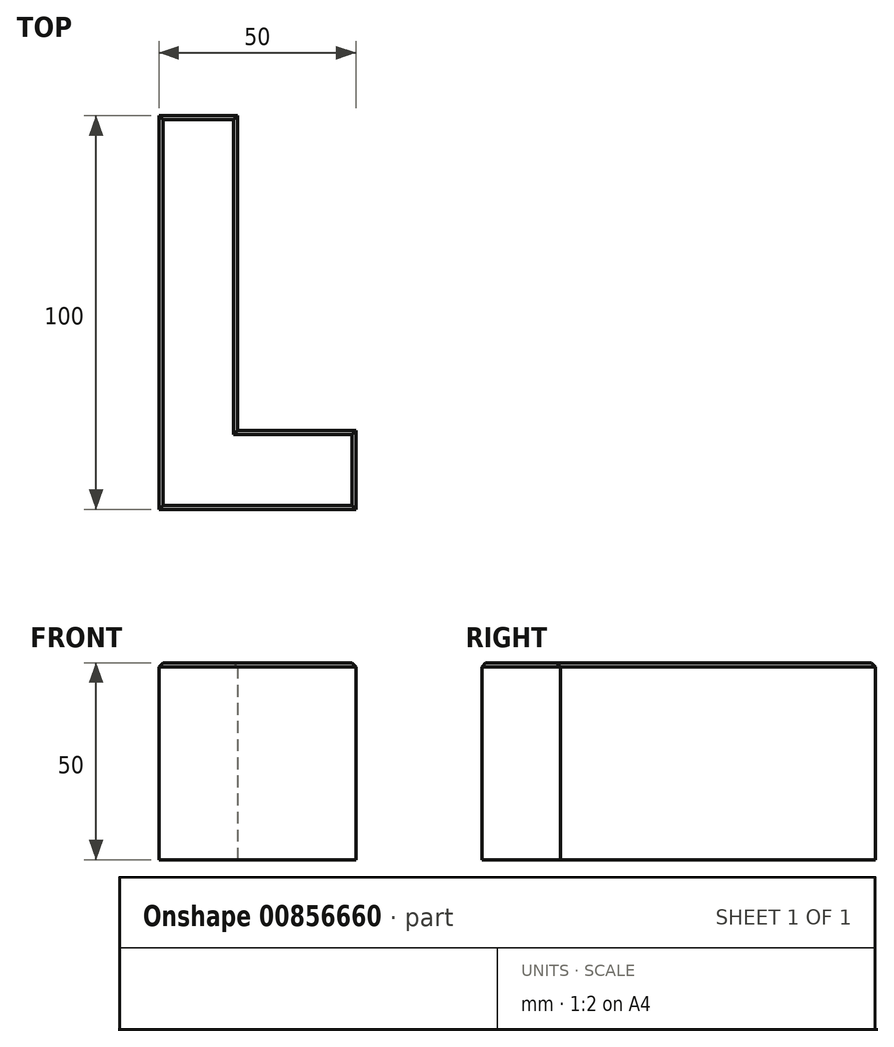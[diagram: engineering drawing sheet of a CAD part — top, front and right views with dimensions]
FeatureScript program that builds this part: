
annotation { "Feature Type Name" : "Feature", "Feature Type Description" : "" }
export const myFeature = defineFeature(function(context is Context, id is Id, definition is map)
    precondition{}
    {
        {
            var Q0;
            Q0=qCreatedBy(makeId("Top.planeOp"),FACE);
            var sketch = newSketch(context, id + "F0", { "sketchPlane" : qUnion([Q0])});
            skLineSegment(sketch, "E0", {"start": v(-67.67, -40.21) * mm, "end": v(-17.67, -40.21) * mm});
            skLineSegment(sketch, "E1", {"start": v(-67.67, -40.21) * mm, "end": v(-67.67, 59.79) * mm});
            skLineSegment(sketch, "E2", {"start": v(-17.67, -40.21) * mm, "end": v(-17.67, -20.21) * mm});
            skLineSegment(sketch, "E3", {"start": v(-67.67, 59.79) * mm, "end": v(-47.67, 59.79) * mm});
            skLineSegment(sketch, "E4", {"start": v(-47.67, 59.79) * mm, "end": v(-47.67, -20.21) * mm});
            skLineSegment(sketch, "E5", {"start": v(-17.67, -20.21) * mm, "end": v(-47.67, -20.21) * mm});
            skSolve(sketch);
        }
        {
            var Q0;
            Q0=makeQuery(id+"F0.imprint","IMPRINT",FACE,{"disambiguationData":[TD([[makeQuery(id+"F0.imprint","IMPRINT",EDGE,{"derivedFrom":sQuery(id+"F0.wireOp",EDGE,"E0")}),1.0]])]});
            extrude(context, id + "F1", {"entities" : qUnion([Q0]), "depth" : 50 * mm, "offsetDistance" : 25 * mm});
        }
        {
            var Q0;
            Q0=makeQuery(id+"F1.opExtrude","CAP_EDGE",EDGE,{"disambiguationData":[OSD([sQuery(id+"F0.wireOp",EDGE,"E3")])],"isStart":false});
            var Q1;
            Q1=makeQuery(id+"F1.opExtrude","CAP_EDGE",EDGE,{"disambiguationData":[OSD([sQuery(id+"F0.wireOp",EDGE,"E4")])],"isStart":false});
            var Q2;
            Q2=makeQuery(id+"F1.opExtrude","CAP_EDGE",EDGE,{"disambiguationData":[OSD([sQuery(id+"F0.wireOp",EDGE,"E1")])],"isStart":false});
            var Q3;
            Q3=makeQuery(id+"F1.opExtrude","CAP_FACE",FACE,{"disambiguationData":[OSD([sQuery(id+"F0.wireOp",EDGE,"E0"),sQuery(id+"F0.wireOp",EDGE,"E1"),sQuery(id+"F0.wireOp",EDGE,"E2"),sQuery(id+"F0.wireOp",EDGE,"E3"),sQuery(id+"F0.wireOp",EDGE,"E4"),sQuery(id+"F0.wireOp",EDGE,"E5")])],"isStart":false});
            chamfer(context, id + "F2", {"entities" : qUnion([Q0, Q1, Q2, Q3]), "width" : 1 * mm, "tangentPropagation" : true});
        }
    });
